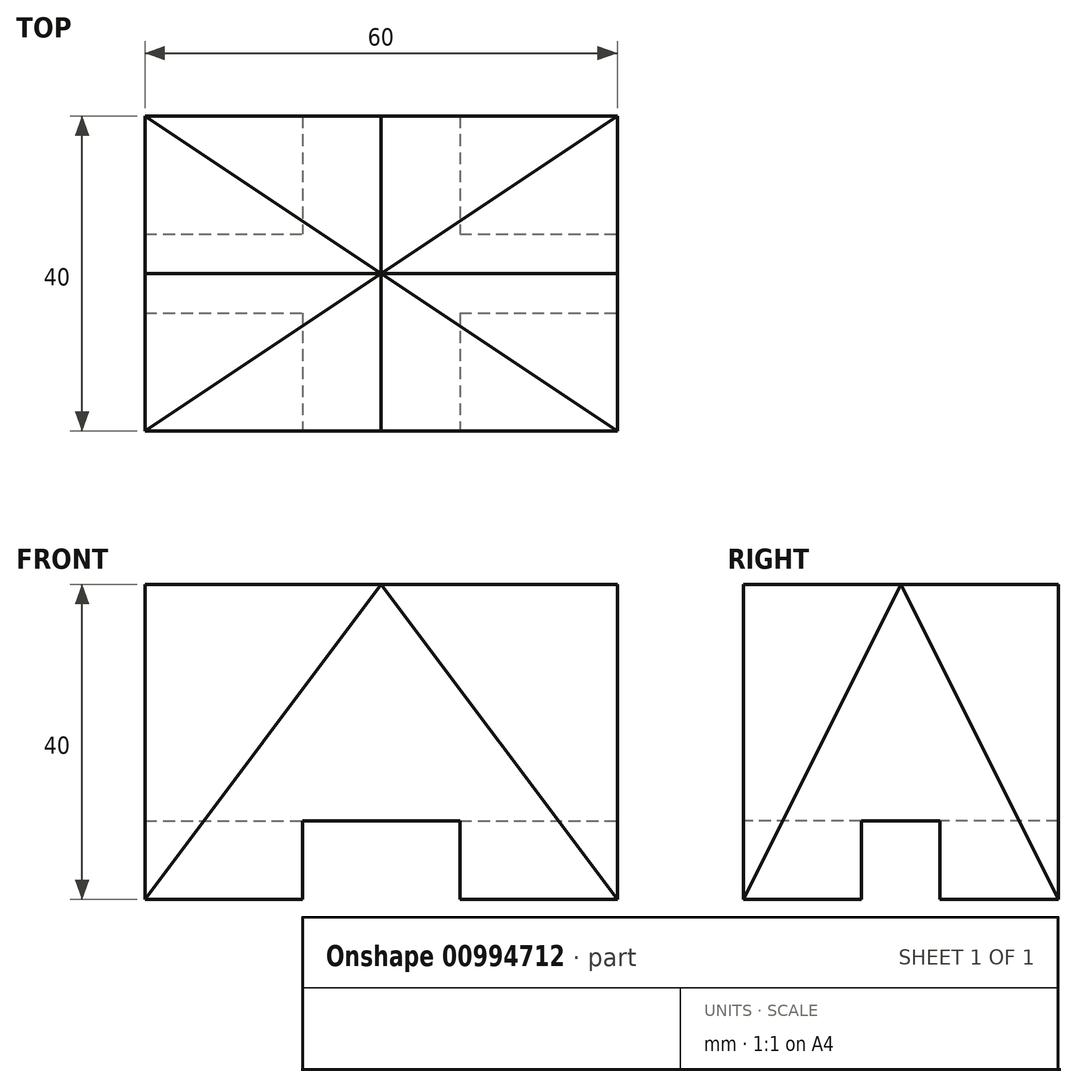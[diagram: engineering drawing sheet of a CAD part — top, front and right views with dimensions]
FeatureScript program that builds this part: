
annotation { "Feature Type Name" : "Feature", "Feature Type Description" : "" }
export const myFeature = defineFeature(function(context is Context, id is Id, definition is map)
    precondition{}
    {
        {
            var Q0;
            Q0=qCreatedBy(makeId("Front.planeOp"),FACE);
            var sketch = newSketch(context, id + "F0", { "sketchPlane" : qUnion([Q0])});
            skLineSegment(sketch, "E0", {"start": v(-30, 0) * mm, "end": v(30, 0) * mm});
            skLineSegment(sketch, "E1", {"start": v(30, 0) * mm, "end": v(0, 40) * mm});
            skLineSegment(sketch, "E2", {"start": v(0, 40) * mm, "end": v(-30, 0) * mm});
            skSolve(sketch);
        }
        {
            var Q0;
            Q0 = qSketchRegion(id + "F0", true);
            extrude(context, id + "F1", {"entities" : qUnion([Q0]), "endBound" : BoundingType.SYMMETRIC, "depth" : 40 * mm, "offsetDistance" : 25 * mm});
        }
        {
            var Q0;
            Q0=qCreatedBy(makeId("Right.planeOp"),FACE);
            var sketch = newSketch(context, id + "F2", { "sketchPlane" : qUnion([Q0])});
            skLineSegment(sketch, "E3", {"start": v(0, 40) * mm, "end": v(-20, 0) * mm});
            skLineSegment(sketch, "E4", {"start": v(-20, 0) * mm, "end": v(20, 0) * mm});
            skLineSegment(sketch, "E5", {"start": v(20, 0) * mm, "end": v(0, 40) * mm});
            skSolve(sketch);
        }
        {
            var Q0;
            Q0 = qSketchRegion(id + "F2", true);
            extrude(context, id + "F3", {"entities" : qUnion([Q0]), "operationType" : NewBodyOperationType.ADD, "endBound" : BoundingType.SYMMETRIC, "depth" : 60 * mm, "offsetDistance" : 25 * mm});
        }
        {
            var Q0;
            Q0=makeQuery(id+"F1.opExtrude","CAP_FACE",FACE,{"disambiguationData":[OSD([sQuery(id+"F0.wireOp",EDGE,"E0"),sQuery(id+"F0.wireOp",EDGE,"E1"),sQuery(id+"F0.wireOp",EDGE,"E2")])],"isStart":false});
            var sketch = newSketch(context, id + "F4", { "sketchPlane" : qUnion([Q0])});
            skLineSegment(sketch, "E6.bottom", {"start": v(-10, 0) * mm, "end": v(10, 0) * mm});
            skLineSegment(sketch, "E6.top", {"start": v(-10, 10) * mm, "end": v(10, 10) * mm});
            skLineSegment(sketch, "E6.left", {"start": v(-10, 0) * mm, "end": v(-10, 10) * mm});
            skLineSegment(sketch, "E6.right", {"start": v(10, 0) * mm, "end": v(10, 10) * mm});
            skSolve(sketch);
        }
        {
            var Q0;
            Q0 = qSketchRegion(id + "F4", true);
            var Q1;
            Q1=makeQuery(id+"F1.opExtrude","CAP_FACE",FACE,{"disambiguationData":[OSD([sQuery(id+"F0.wireOp",EDGE,"E0"),sQuery(id+"F0.wireOp",EDGE,"E1"),sQuery(id+"F0.wireOp",EDGE,"E2")])],"isStart":true});
            extrude(context, id + "F5", {"entities" : qUnion([Q0]), "operationType" : NewBodyOperationType.REMOVE, "endBound" : BoundingType.UP_TO_SURFACE, "oppositeDirection" : true, "depth" : 25 * mm, "endBoundEntityFace" : qUnion([Q1]), "offsetDistance" : 25 * mm});
        }
        {
            var Q0;
            Q0=makeQuery(id+"F3.opExtrude","CAP_FACE",FACE,{"disambiguationData":[OSD([sQuery(id+"F2.wireOp",EDGE,"E3"),sQuery(id+"F2.wireOp",EDGE,"E4"),sQuery(id+"F2.wireOp",EDGE,"E5")])],"isStart":false});
            var sketch = newSketch(context, id + "F6", { "sketchPlane" : qUnion([Q0])});
            skLineSegment(sketch, "E7.bottom", {"start": v(-5, 0) * mm, "end": v(5, 0) * mm});
            skLineSegment(sketch, "E7.top", {"start": v(-5, 10) * mm, "end": v(5, 10) * mm});
            skLineSegment(sketch, "E7.left", {"start": v(-5, 0) * mm, "end": v(-5, 10) * mm});
            skLineSegment(sketch, "E7.right", {"start": v(5, 0) * mm, "end": v(5, 10) * mm});
            skSolve(sketch);
        }
        {
            var Q0;
            Q0 = qSketchRegion(id + "F6", true);
            extrude(context, id + "F7", {"entities" : qUnion([Q0]), "operationType" : NewBodyOperationType.REMOVE, "oppositeDirection" : true, "depth" : 64.9 * mm, "offsetDistance" : 25 * mm});
        }
    });
